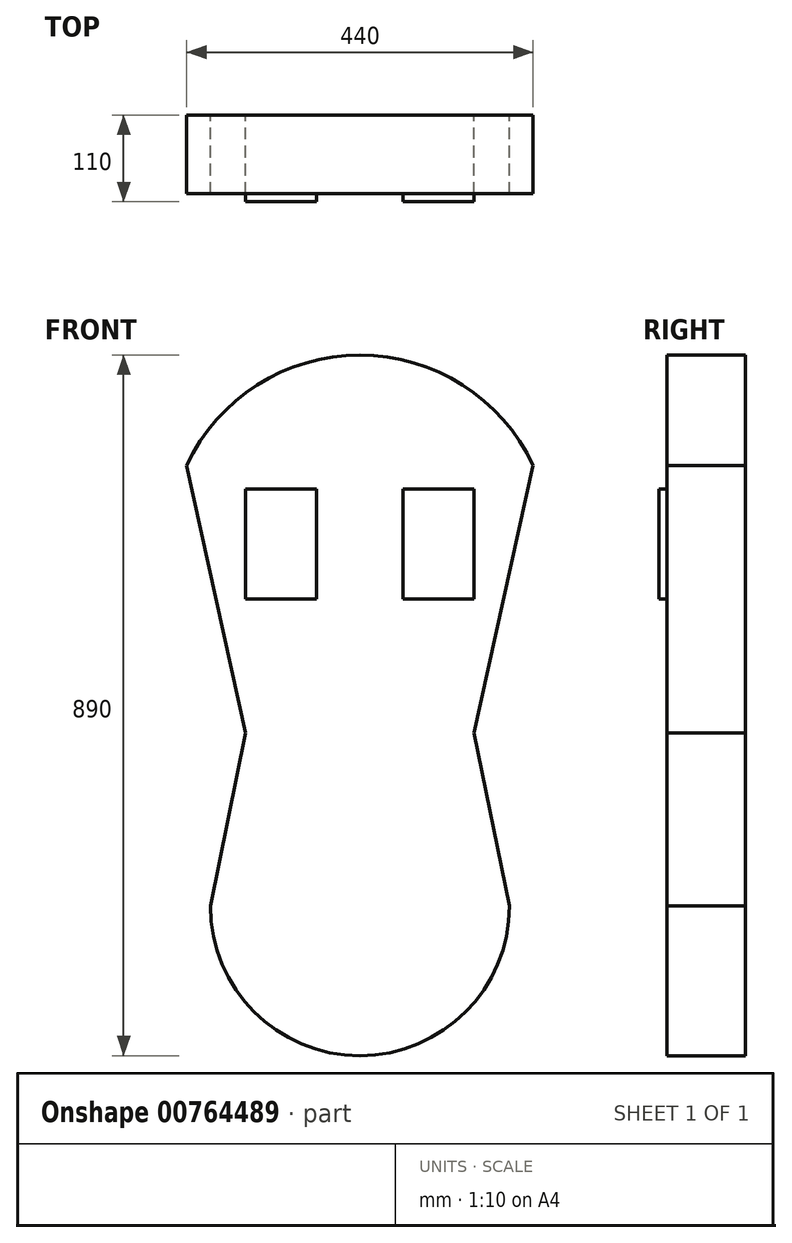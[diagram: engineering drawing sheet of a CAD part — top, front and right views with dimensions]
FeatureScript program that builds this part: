
annotation { "Feature Type Name" : "Feature", "Feature Type Description" : "" }
export const myFeature = defineFeature(function(context is Context, id is Id, definition is map)
    precondition{}
    {
        {
            var Q0;
            Q0=qCreatedBy(makeId("Front.planeOp"),FACE);
            var sketch = newSketch(context, id + "F0", { "sketchPlane" : qUnion([Q0])});
            skArc(sketch, "E0", {"start": v(220, 340) * mm, "mid": v(0, 480) * mm, "end": v(-220, 340) * mm});
            skArc(sketch, "E1", {"start": v(-190, -220) * mm, "mid": v(0, -410) * mm, "end": v(190, -220) * mm});
            skLineSegment(sketch, "E2", {"start": v(-220, 340) * mm, "end": v(-145, 0) * mm});
            skLineSegment(sketch, "E3", {"start": v(-145, 0) * mm, "end": v(-190, -220) * mm});
            skLineSegment(sketch, "E4", {"start": v(220, 340) * mm, "end": v(145, 0) * mm});
            skLineSegment(sketch, "E5", {"start": v(145, 0) * mm, "end": v(190, -220) * mm});
            skPoint(sketch, "E6.start.orphan", {"position": v(0, -410) * mm});
            skLineSegment(sketch, "E7", {"start": v(-220, 340) * mm, "end": v(220, 340) * mm, "construction": true});
            skLineSegment(sketch, "E8", {"start": v(-145, 0) * mm, "end": v(145, 0) * mm, "construction": true});
            skLineSegment(sketch, "E9", {"start": v(-190, -220) * mm, "end": v(190, -220) * mm, "construction": true});
            skCircle(sketch, "E10", {"center": v(-128.45, -360) * mm, "radius": 50 * mm});
            skCircle(sketch, "E11", {"center": v(128.45, -360) * mm, "radius": 50 * mm});
            skCircle(sketch, "E12", {"center": v(-220, 340) * mm, "radius": 50 * mm});
            skArc(sketch, "E13", {"start": v(220.1, 290) * mm, "mid": v(270, 340) * mm, "end": v(220.1, 390) * mm});
            skLineSegment(sketch, "E14", {"start": v(-128.45, -360) * mm, "end": v(128.45, -360) * mm, "construction": true});
            skLineSegment(sketch, "E15.bottom", {"start": v(55, 310) * mm, "end": v(145, 310) * mm});
            skLineSegment(sketch, "E15.top", {"start": v(55, 170) * mm, "end": v(145, 170) * mm});
            skLineSegment(sketch, "E15.left", {"start": v(55, 310) * mm, "end": v(55, 170) * mm});
            skLineSegment(sketch, "E15.right", {"start": v(145, 310) * mm, "end": v(145, 170) * mm});
            skPoint(sketch, "E15.middle", {"position": v(100, 240) * mm});
            skLineSegment(sketch, "E16.MirrorCS", {"start": v(-55, 310) * mm, "end": v(-55, 170) * mm});
            skLineSegment(sketch, "E17.MirrorCS", {"start": v(-55, 310) * mm, "end": v(-145, 310) * mm});
            skLineSegment(sketch, "E18.MirrorCS", {"start": v(-145, 310) * mm, "end": v(-145, 170) * mm});
            skLineSegment(sketch, "E19.MirrorCS", {"start": v(-55, 170) * mm, "end": v(-145, 170) * mm});
            skPoint(sketch, "E20.MirrorP", {"position": v(-100, 240) * mm});
            skLineSegment(sketch, "E21", {"start": v(-219.5, 390) * mm, "end": v(-219.5, 290) * mm, "construction": true});
            skLineSegment(sketch, "E22", {"start": v(-129.03, -310) * mm, "end": v(-129.03, -410) * mm, "construction": true});
            skLineSegment(sketch, "E23", {"start": v(130.4, -310.04) * mm, "end": v(130.4, -409.96) * mm, "construction": true});
            skLineSegment(sketch, "E24", {"start": v(220.1, 390) * mm, "end": v(220.1, 290) * mm, "construction": true});
            skSolve(sketch);
        }
        {
            var Q0;
            {var subQ0=sQuery(id+"F0.wireOp",EDGE,"E10");var subQ1=sQuery(id+"F0.wireOp",EDGE,"E1");var subQ2=makeQuery(id+"F0.imprint","INTERSECT",VERTEX,{"disambiguationData":[OD(0.0)],"derivedFrom":[subQ1,subQ0]});Q0=makeQuery(id+"F0.imprint","IMPRINT",FACE,{"disambiguationData":[TD([[makeQuery(id+"F0.imprint","IMPRINT",EDGE,{"disambiguationData":[TD([[subQ2,-1.0]])],"derivedFrom":subQ1}),1.0]])]});}
            var Q1;
            {var subQ0=sQuery(id+"F0.wireOp",EDGE,"E11");var subQ1=sQuery(id+"F0.wireOp",EDGE,"E1");var subQ2=makeQuery(id+"F0.imprint","INTERSECT",VERTEX,{"disambiguationData":[OD(0.0)],"derivedFrom":[subQ1,subQ0]});Q1=makeQuery(id+"F0.imprint","IMPRINT",FACE,{"disambiguationData":[TD([[makeQuery(id+"F0.imprint","IMPRINT",EDGE,{"disambiguationData":[TD([[subQ2,-1.0]])],"derivedFrom":subQ1}),1.0]])]});}
            var Q2;
            {var subQ0=sQuery(id+"F0.wireOp",EDGE,"E4");var subQ1=sQuery(id+"F0.wireOp",EDGE,"E0");var subQ2=makeQuery(id+"F0.imprint","INTERSECT",VERTEX,{"derivedFrom":[subQ1,subQ0]});Q2=makeQuery(id+"F0.imprint","IMPRINT",FACE,{"disambiguationData":[TD([[makeQuery(id+"F0.imprint","IMPRINT",EDGE,{"disambiguationData":[TD([[subQ2,-1.0]])],"derivedFrom":subQ1}),1.0]])]});}
            var Q3;
            {var subQ0=sQuery(id+"F0.wireOp",EDGE,"E2");var subQ1=sQuery(id+"F0.wireOp",EDGE,"E0");var subQ2=makeQuery(id+"F0.imprint","INTERSECT",VERTEX,{"derivedFrom":[subQ1,subQ0]});Q3=makeQuery(id+"F0.imprint","IMPRINT",FACE,{"disambiguationData":[TD([[makeQuery(id+"F0.imprint","IMPRINT",EDGE,{"disambiguationData":[TD([[subQ2,1.0]])],"derivedFrom":subQ1}),1.0]])]});}
            var Q4;
            {var subQ5=sQuery(id+"F0.wireOp",EDGE,"E3");Q4=makeQuery(id+"F0.imprint","IMPRINT",FACE,{"disambiguationData":[TD([[makeQuery(id+"F0.imprint","IMPRINT",EDGE,{"derivedFrom":subQ5}),1.0]])]});}
            var Q5;
            Q5=makeQuery(id+"F0.imprint","IMPRINT",FACE,{"disambiguationData":[TD([[makeQuery(id+"F0.imprint","IMPRINT",EDGE,{"derivedFrom":sQuery(id+"F0.wireOp",EDGE,"E16.MirrorCS")}),-1.0]])]});
            var Q6;
            Q6=makeQuery(id+"F0.imprint","IMPRINT",FACE,{"disambiguationData":[TD([[makeQuery(id+"F0.imprint","IMPRINT",EDGE,{"derivedFrom":sQuery(id+"F0.wireOp",EDGE,"E15.bottom")}),-1.0]])]});
            extrude(context, id + "F1", {"entities" : qUnion([Q0, Q1, Q2, Q3, Q4, Q5, Q6]), "endBound" : BoundingType.SYMMETRIC, "depth" : 100 * mm, "offsetDistance" : 25 * mm});
        }
        {
            var Q0;
            Q0=makeQuery(id+"F0.imprint","IMPRINT",FACE,{"disambiguationData":[TD([[makeQuery(id+"F0.imprint","IMPRINT",EDGE,{"derivedFrom":sQuery(id+"F0.wireOp",EDGE,"E16.MirrorCS")}),-1.0]])]});
            var Q1;
            Q1=makeQuery(id+"F0.imprint","IMPRINT",FACE,{"disambiguationData":[TD([[makeQuery(id+"F0.imprint","IMPRINT",EDGE,{"derivedFrom":sQuery(id+"F0.wireOp",EDGE,"E15.bottom")}),-1.0]])]});
            extrude(context, id + "F2", {"entities" : qUnion([Q0, Q1]), "operationType" : NewBodyOperationType.ADD, "depth" : 60 * mm, "offsetDistance" : 25 * mm});
        }
    });
